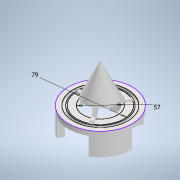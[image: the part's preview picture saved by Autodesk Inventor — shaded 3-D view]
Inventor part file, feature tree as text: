
AUTODESK INVENTOR PART (.ipt)
format: ipt  version: 2022.4 (Build 264492010, 492A)  size: 236,544 bytes
history: native  units: mm
features: sketch x7, extrude x5, revolve x1, plane x1, pattern_circular x1
ambient origin geometry x8: Origin, YZ Plane, XZ Plane, XY Plane, X Axis, Y Axis, Z Axis, Center Point
bodies: Solid1 (feature_tree)
feature tree (15):
  revolve  "Revolution1"  [1 undecoded]
  plane  "Work Plane1"
  extrude  "Extrusion1"  [1 undecoded]
  extrude  "Extrusion2"  Depth=82.5mm
  pattern_circular  "Circular Pattern1"  Count=3 Angle=360.0deg
  sketch  "Sketch5"  dims[d9=8.0mm d10=0.0mm]
  extrude  "Extrusion3"  Depth=57.0mm
  extrude  "Extrusion4"  Depth=25.0mm
  extrude  "Extrusion5"  Depth=30.0mm
  sketch  "Sketch1"  dims[d1=60.0mm d2=13.0mm]
  sketch  "Sketch3"  dims[d3=90.0deg d6=-5.0mm]
  sketch  "Sketch4"  dims[d7=50.0mm d8=82.5mm]
  sketch  "Sketch6"  dims[d11=5.0mm d12=0.0mm d13=30.0mm d14=360.0deg]
  sketch  "Sketch7"  dims[d16=79.0mm d17=57.0mm]
  sketch  "Sketch8"  dims[d18=5.0mm d19=25.0mm d20=82.5mm d21=4.5mm d22=8.0mm d23=0.0mm d24=4.0mm d25=0.0mm d26=0.0mm d27=10.0mm d28=120.0deg d29=120.0deg d30=120.0deg d31=30.0mm d32=0.0mm]
note: 2 required parameter values undecoded (feature->parameter linkage not recoverable at this tier; creation-order binding heuristic only, values carry confidence <= 0.55)